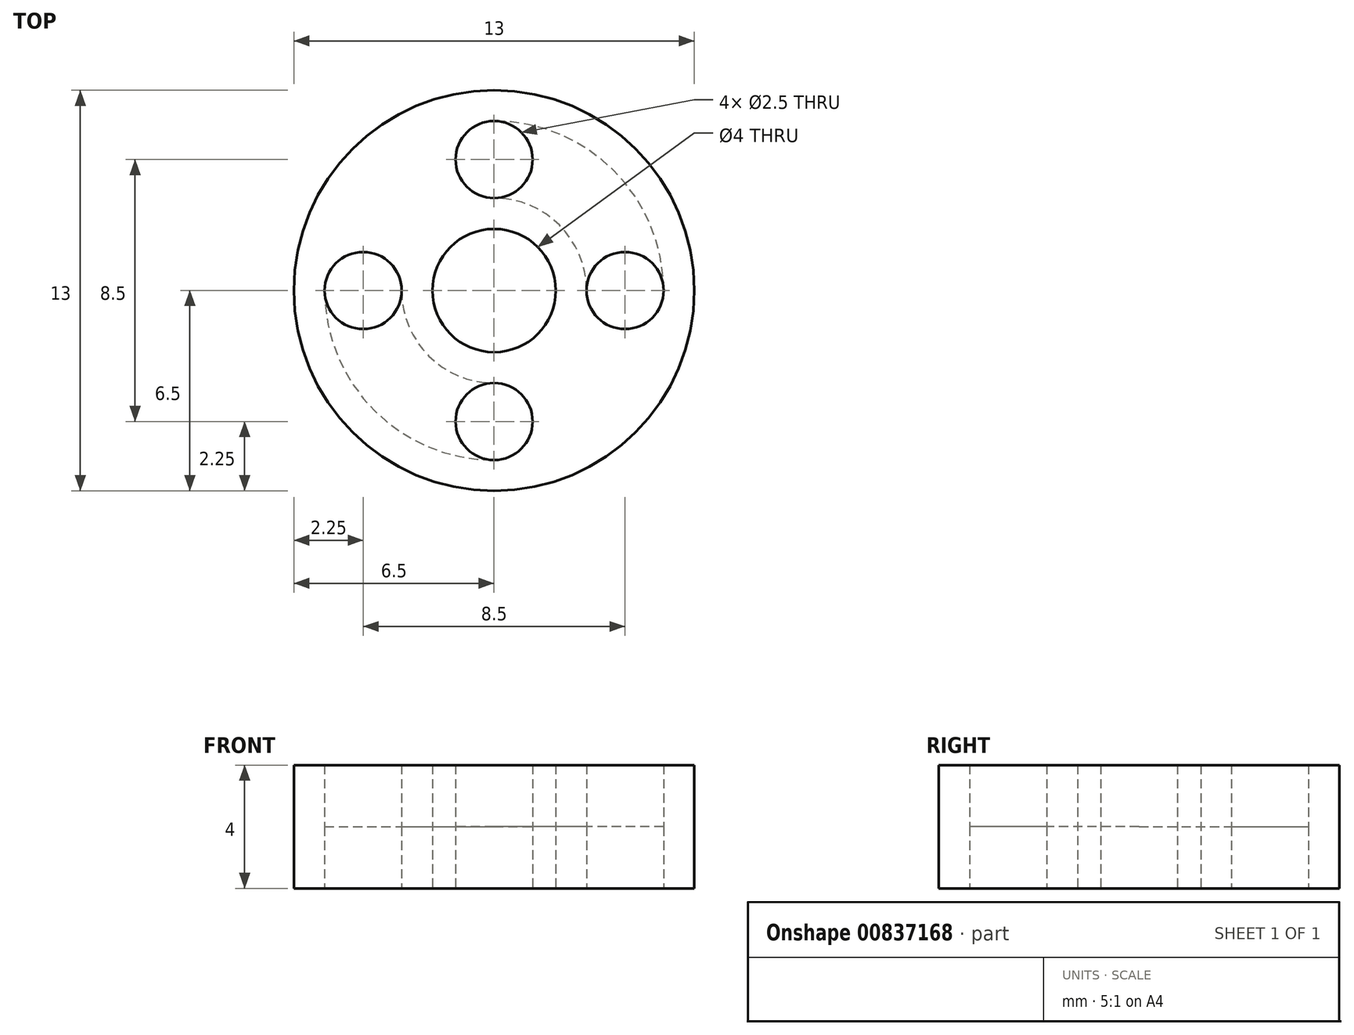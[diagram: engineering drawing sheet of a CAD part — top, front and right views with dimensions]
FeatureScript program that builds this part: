
annotation { "Feature Type Name" : "Feature", "Feature Type Description" : "" }
export const myFeature = defineFeature(function(context is Context, id is Id, definition is map)
    precondition{}
    {
        {
            var Q0;
            Q0=qCreatedBy(makeId("Top.planeOp"),FACE);
            var sketch = newSketch(context, id + "F0", { "sketchPlane" : qUnion([Q0])});
            skLineSegment(sketch, "E0.bottom", {"start": v(0, 0) * mm, "end": v(20, 0) * mm});
            skLineSegment(sketch, "E0.top", {"start": v(0, -20) * mm, "end": v(20, -20) * mm});
            skLineSegment(sketch, "E0.left", {"start": v(0, 0) * mm, "end": v(0, -20) * mm});
            skLineSegment(sketch, "E0.right", {"start": v(20, 0) * mm, "end": v(20, -20) * mm});
            skLineSegment(sketch, "E1", {"start": v(0, -10) * mm, "end": v(20, -10) * mm, "construction": true});
            skCircle(sketch, "E2", {"center": v(10, -10) * mm, "radius": 2 * mm});
            skCircle(sketch, "E3", {"center": v(10, -10) * mm, "radius": 5.5 * mm});
            skCircle(sketch, "E4", {"center": v(10, -10) * mm, "radius": 6.5 * mm});
            skCircle(sketch, "E5", {"center": v(10, -10) * mm, "radius": 7 * mm});
            skCircle(sketch, "E6", {"center": v(10, -10) * mm, "radius": 8.5 * mm});
            skCircle(sketch, "E7", {"center": v(10, -10) * mm, "radius": 3 * mm});
            skLineSegment(sketch, "E8", {"start": v(10, -10) * mm, "end": v(10, -5.75) * mm, "construction": true});
            skCircle(sketch, "E9", {"center": v(10, -5.75) * mm, "radius": 1.25 * mm});
            skCircle(sketch, "E10.1.0", {"center": v(5.75, -10) * mm, "radius": 1.25 * mm});
            skCircle(sketch, "E10.2.0", {"center": v(10, -14.25) * mm, "radius": 1.25 * mm});
            skCircle(sketch, "E10.3.0", {"center": v(14.25, -10) * mm, "radius": 1.25 * mm});
            skLineSegment(sketch, "E11", {"start": v(0, -2.5) * mm, "end": v(2.5, -2.5) * mm, "construction": true});
            skLineSegment(sketch, "E12", {"start": v(2.5, -2.5) * mm, "end": v(2.5, 0) * mm, "construction": true});
            skCircle(sketch, "E13", {"center": v(2.5, -2.5) * mm, "radius": 1 * mm});
            skCircle(sketch, "E14.1.0", {"center": v(2.5, -17.5) * mm, "radius": 1 * mm});
            skCircle(sketch, "E14.2.0", {"center": v(17.5, -17.5) * mm, "radius": 1 * mm});
            skCircle(sketch, "E14.3.0", {"center": v(17.5, -2.5) * mm, "radius": 1 * mm});
            skSolve(sketch);
        }
        {
            var Q0;
            Q0=makeQuery(id+"F0.imprint","IMPRINT",FACE,{"disambiguationData":[TD([[makeQuery(id+"F0.imprint","IMPRINT",EDGE,{"derivedFrom":sQuery(id+"F0.wireOp",EDGE,"E4")}),1.0]])]});
            var Q1;
            Q1=makeQuery(id+"F0.imprint","IMPRINT",FACE,{"disambiguationData":[TD([[makeQuery(id+"F0.imprint","IMPRINT",EDGE,{"derivedFrom":sQuery(id+"F0.wireOp",EDGE,"E2")}),-1.0]])]});
            var Q2;
            {var subQ0=sQuery(id+"F0.wireOp",EDGE,"E9");var subQ1=sQuery(id+"F0.wireOp",EDGE,"E3");var subQ2=makeQuery(id+"F0.imprint","INTERSECT",VERTEX,{"derivedFrom":[subQ1,subQ0]});Q2=makeQuery(id+"F0.imprint","IMPRINT",FACE,{"disambiguationData":[TD([[makeQuery(id+"F0.imprint","IMPRINT",EDGE,{"disambiguationData":[TD([[subQ2,-1.0]])],"derivedFrom":subQ1}),1.0]])]});}
            var Q3;
            {var subQ0=sQuery(id+"F0.wireOp",EDGE,"E10.3.0");var subQ1=sQuery(id+"F0.wireOp",EDGE,"E3");var subQ2=makeQuery(id+"F0.imprint","INTERSECT",VERTEX,{"derivedFrom":[subQ1,subQ0]});Q3=makeQuery(id+"F0.imprint","IMPRINT",FACE,{"disambiguationData":[TD([[makeQuery(id+"F0.imprint","IMPRINT",EDGE,{"disambiguationData":[TD([[subQ2,1.0]])],"derivedFrom":subQ1}),1.0]])]});}
            var Q4;
            {var subQ0=sQuery(id+"F0.wireOp",EDGE,"E10.1.0");var subQ1=sQuery(id+"F0.wireOp",EDGE,"E3");var subQ2=makeQuery(id+"F0.imprint","INTERSECT",VERTEX,{"derivedFrom":[subQ1,subQ0]});Q4=makeQuery(id+"F0.imprint","IMPRINT",FACE,{"disambiguationData":[TD([[makeQuery(id+"F0.imprint","IMPRINT",EDGE,{"disambiguationData":[TD([[subQ2,-1.0]])],"derivedFrom":subQ1}),1.0]])]});}
            var Q5;
            {var subQ0=sQuery(id+"F0.wireOp",EDGE,"E9");var subQ1=sQuery(id+"F0.wireOp",EDGE,"E3");var subQ2=makeQuery(id+"F0.imprint","INTERSECT",VERTEX,{"derivedFrom":[subQ1,subQ0]});Q5=makeQuery(id+"F0.imprint","IMPRINT",FACE,{"disambiguationData":[TD([[makeQuery(id+"F0.imprint","IMPRINT",EDGE,{"disambiguationData":[TD([[subQ2,1.0]])],"derivedFrom":subQ1}),1.0]])]});}
            extrude(context, id + "F1", {"entities" : qUnion([Q0, Q1, Q2, Q3, Q4, Q5]), "depth" : 4 * mm, "offsetDistance" : 25 * mm});
        }
        {
            var Q0;
            {var subQ0=sQuery(id+"F0.wireOp",EDGE,"E10.1.0");var subQ1=sQuery(id+"F0.wireOp",EDGE,"E3");var subQ2=makeQuery(id+"F0.imprint","INTERSECT",VERTEX,{"derivedFrom":[subQ1,subQ0]});Q0=makeQuery(id+"F0.imprint","IMPRINT",FACE,{"disambiguationData":[TD([[makeQuery(id+"F0.imprint","IMPRINT",EDGE,{"disambiguationData":[TD([[subQ2,-1.0]])],"derivedFrom":subQ1}),1.0]])]});}
            var Q1;
            {var subQ0=sQuery(id+"F0.wireOp",EDGE,"E9");var subQ1=sQuery(id+"F0.wireOp",EDGE,"E3");var subQ2=makeQuery(id+"F0.imprint","INTERSECT",VERTEX,{"derivedFrom":[subQ1,subQ0]});Q1=makeQuery(id+"F0.imprint","IMPRINT",FACE,{"disambiguationData":[TD([[makeQuery(id+"F0.imprint","IMPRINT",EDGE,{"disambiguationData":[TD([[subQ2,1.0]])],"derivedFrom":subQ1}),1.0]])]});}
            extrude(context, id + "F2", {"entities" : qUnion([Q0, Q1]), "operationType" : NewBodyOperationType.REMOVE, "depth" : 2 * mm, "offsetDistance" : 25 * mm});
        }
    });
